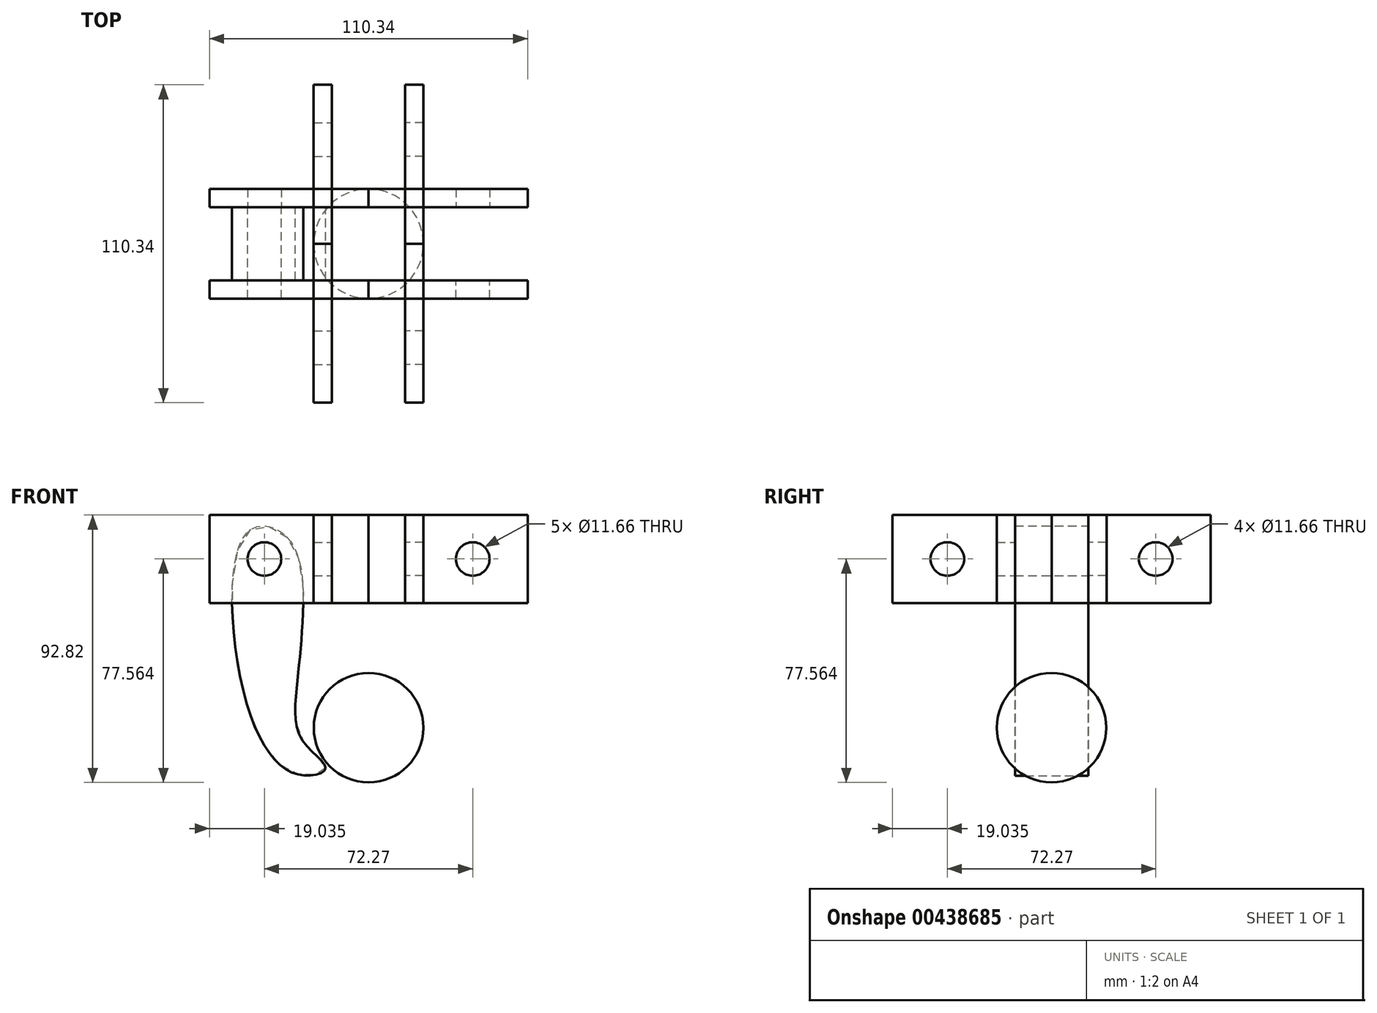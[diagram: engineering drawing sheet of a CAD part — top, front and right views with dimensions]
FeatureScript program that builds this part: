
annotation { "Feature Type Name" : "Feature", "Feature Type Description" : "" }
export const myFeature = defineFeature(function(context is Context, id is Id, definition is map)
    precondition{}
    {
        {
            var Q0;
            Q0=qCreatedBy(makeId("Front.planeOp"),FACE);
            var sketch = newSketch(context, id + "F0", { "sketchPlane" : qUnion([Q0])});
            skCircle(sketch, "E0", {"center": v(0, 0) * mm, "radius": 19 * mm});
            skFitSpline(sketch, "E1", {"points": [v(-14.93, -14.05) * mm, v(-23.3, -16.5) * mm, v(-41.12, 4.81) * mm, v(-42.17, 67.68) * mm, v(-27.83, 65.62) * mm, v(-22.84, 37.8) * mm, v(-24.92, 14.12) * mm, v(-22.84, -4.57) * mm, v(-14.93, -14.05) * mm]});
            skCircle(sketch, "E2", {"center": v(-36.14, 58.56) * mm, "radius": 5.83 * mm});
            skSolve(sketch);
        }
        {
            var Q0;
            Q0=makeQuery(id+"F0.imprint","IMPRINT",FACE,{"disambiguationData":[TD([[makeQuery(id+"F0.imprint","IMPRINT",EDGE,{"derivedFrom":sQuery(id+"F0.wireOp",EDGE,"E1")}),-1.0]])]});
            extrude(context, id + "F1", {"entities" : qUnion([Q0]), "endBound" : BoundingType.SYMMETRIC, "depth" : 25.4 * mm});
        }
        {
            var Q0;
            Q0=makeQuery(id+"F1.opExtrude","CAP_FACE",FACE,{"disambiguationData":[OSD([sQuery(id+"F0.wireOp",EDGE,"E1"),sQuery(id+"F0.wireOp",EDGE,"E2")])],"isStart":false});
            var sketch = newSketch(context, id + "F2", { "sketchPlane" : qUnion([Q0])});
            skLineSegment(sketch, "E3.bottom", {"start": v(-55.17, 73.82) * mm, "end": v(0, 73.82) * mm});
            skLineSegment(sketch, "E3.top", {"start": v(-55.17, 43.28) * mm, "end": v(0, 43.28) * mm});
            skLineSegment(sketch, "E3.left", {"start": v(-55.17, 73.82) * mm, "end": v(-55.17, 43.28) * mm});
            skLineSegment(sketch, "E3.right", {"start": v(0, 73.82) * mm, "end": v(0, 43.28) * mm});
            skSolve(sketch);
        }
        {
            var Q0;
            Q0=makeQuery(id+"F2.imprint","IMPRINT",FACE,{"disambiguationData":[TD([[makeQuery(id+"F2.imprint","IMPRINT",EDGE,{"derivedFrom":makeQuery(id+"F1.opExtrude","CAP_EDGE",EDGE,{"disambiguationData":[OSD([sQuery(id+"F0.wireOp",EDGE,"E2")])],"isStart":false})}),-1.0]])]});
            var Q1;
            Q1=makeQuery(id+"F2.imprint","IMPRINT",FACE,{"disambiguationData":[TD([[makeQuery(id+"F2.imprint","IMPRINT",EDGE,{"derivedFrom":sQuery(id+"F2.wireOp",EDGE,"E3.bottom")}),-1.0]])]});
            extrude(context, id + "F3", {"entities" : qUnion([Q0, Q1]), "depth" : 6.35 * mm});
        }
        {
            var Q0;
            Q0=makeQuery(id+"F3.opExtrude","SWEPT_BODY",BODY,{"disambiguationData":[OSD([sQuery(id+"F0.wireOp",EDGE,"E2"),sQuery(id+"F2.wireOp",EDGE,"E3.bottom"),sQuery(id+"F2.wireOp",EDGE,"E3.top"),sQuery(id+"F2.wireOp",EDGE,"E3.left"),sQuery(id+"F2.wireOp",EDGE,"E3.right")])]});
            var Q1;
            Q1=qCreatedBy(makeId("Front.planeOp"),FACE);
            mirror(context, id + "F4", {"entities" : qUnion([Q0]), "mirrorPlane" : qUnion([Q1])});
        }
        {
            var Q0;
            Q0=makeQuery(id+"F4.opPattern","COPY",BODY,{"derivedFrom":makeQuery(id+"F3.opExtrude","SWEPT_BODY",BODY,{"disambiguationData":[OSD([sQuery(id+"F0.wireOp",EDGE,"E2"),sQuery(id+"F2.wireOp",EDGE,"E3.bottom"),sQuery(id+"F2.wireOp",EDGE,"E3.top"),sQuery(id+"F2.wireOp",EDGE,"E3.left"),sQuery(id+"F2.wireOp",EDGE,"E3.right")])]}),"instanceName":"1"});
            var Q1;
            Q1=makeQuery(id+"F3.opExtrude","SWEPT_BODY",BODY,{"disambiguationData":[OSD([sQuery(id+"F0.wireOp",EDGE,"E2"),sQuery(id+"F2.wireOp",EDGE,"E3.bottom"),sQuery(id+"F2.wireOp",EDGE,"E3.top"),sQuery(id+"F2.wireOp",EDGE,"E3.left"),sQuery(id+"F2.wireOp",EDGE,"E3.right")])]});
            var Q2;
            Q2=qCreatedBy(makeId("Right.planeOp"),FACE);
            mirror(context, id + "F5", {"entities" : qUnion([Q0, Q1]), "mirrorPlane" : qUnion([Q2])});
        }
        {
            var Q0;
            Q0=qCreatedBy(makeId("Right.planeOp"),FACE);
            var sketch = newSketch(context, id + "F6", { "sketchPlane" : qUnion([Q0])});
            skLineSegment(sketch, "E4", {"start": v(0, -50.6) * mm, "end": v(0, 109.55) * mm});
            skSolve(sketch);
        }
        {
            var Q0;
            Q0=makeQuery(id+"F3.opExtrude","SWEPT_BODY",BODY,{"disambiguationData":[OSD([sQuery(id+"F0.wireOp",EDGE,"E2"),sQuery(id+"F2.wireOp",EDGE,"E3.bottom"),sQuery(id+"F2.wireOp",EDGE,"E3.top"),sQuery(id+"F2.wireOp",EDGE,"E3.left"),sQuery(id+"F2.wireOp",EDGE,"E3.right")])]});
            var Q1;
            Q1=makeQuery(id+"F4.opPattern","COPY",BODY,{"derivedFrom":makeQuery(id+"F3.opExtrude","SWEPT_BODY",BODY,{"disambiguationData":[OSD([sQuery(id+"F0.wireOp",EDGE,"E2"),sQuery(id+"F2.wireOp",EDGE,"E3.bottom"),sQuery(id+"F2.wireOp",EDGE,"E3.top"),sQuery(id+"F2.wireOp",EDGE,"E3.left"),sQuery(id+"F2.wireOp",EDGE,"E3.right")])]}),"instanceName":"1"});
            var Q2;
            Q2=makeQuery(id+"F5.opPattern","COPY",BODY,{"derivedFrom":makeQuery(id+"F4.opPattern","COPY",BODY,{"derivedFrom":makeQuery(id+"F3.opExtrude","SWEPT_BODY",BODY,{"disambiguationData":[OSD([sQuery(id+"F0.wireOp",EDGE,"E2"),sQuery(id+"F2.wireOp",EDGE,"E3.bottom"),sQuery(id+"F2.wireOp",EDGE,"E3.top"),sQuery(id+"F2.wireOp",EDGE,"E3.left"),sQuery(id+"F2.wireOp",EDGE,"E3.right")])]}),"instanceName":"1"}),"instanceName":"1"});
            var Q3;
            Q3=makeQuery(id+"F5.opPattern","COPY",BODY,{"derivedFrom":makeQuery(id+"F3.opExtrude","SWEPT_BODY",BODY,{"disambiguationData":[OSD([sQuery(id+"F0.wireOp",EDGE,"E2"),sQuery(id+"F2.wireOp",EDGE,"E3.bottom"),sQuery(id+"F2.wireOp",EDGE,"E3.top"),sQuery(id+"F2.wireOp",EDGE,"E3.left"),sQuery(id+"F2.wireOp",EDGE,"E3.right")])]}),"instanceName":"1"});
            var Q4;
            Q4=sQuery(id+"F6.wireOp",EDGE,"E4");
            circularPattern(context, id + "F7", {"entities" : qUnion([Q0, Q1, Q2, Q3]), "axis" : qUnion([Q4]), "angle" : 90 * degree, "instanceCount" : 2, "equalSpace" : true});
        }
        {
            var Q0;
            Q0=qCreatedBy(makeId("Front.planeOp"),FACE);
            var sketch = newSketch(context, id + "F8", { "sketchPlane" : qUnion([Q0])});
            skCircle(sketch, "E5.0", {"center": v(0, 0) * mm, "radius": 19 * mm});
            skLineSegment(sketch, "E6", {"start": v(0, 19) * mm, "end": v(0, -19) * mm});
            skSolve(sketch);
        }
        {
            var Q0;
            {var subQ0=sQuery(id+"F8.wireOp",EDGE,"E6");Q0=makeQuery(id+"F8.imprint","IMPRINT",FACE,{"disambiguationData":[TD([[makeQuery(id+"F8.imprint","IMPRINT",EDGE,{"derivedFrom":subQ0}),1.0]])]});}
            var Q1;
            Q1=sQuery(id+"F8.wireOp",EDGE,"E6");
            revolve(context, id + "F9", {"entities" : qUnion([Q0]), "axis" : qUnion([Q1]), "revolveType" : RevolveType.FULL});
        }
    });
